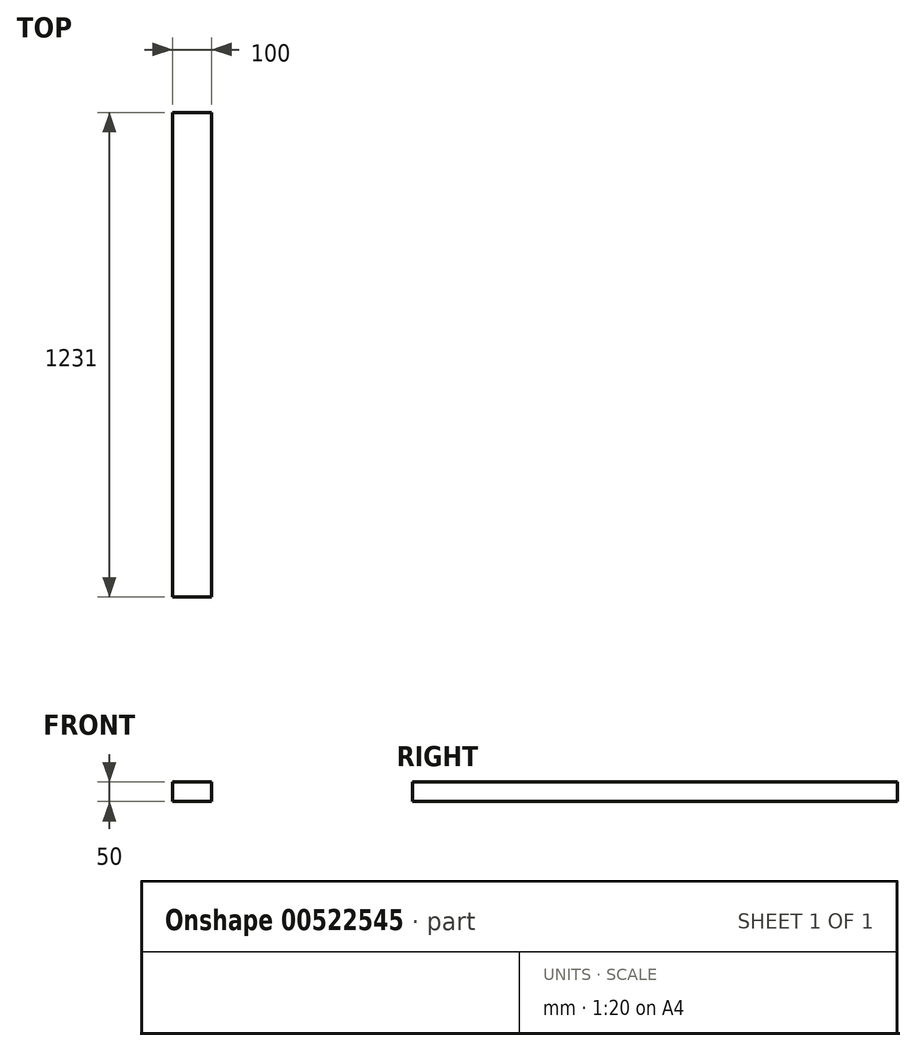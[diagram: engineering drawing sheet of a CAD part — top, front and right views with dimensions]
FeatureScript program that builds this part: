
annotation { "Feature Type Name" : "Feature", "Feature Type Description" : "" }
export const myFeature = defineFeature(function(context is Context, id is Id, definition is map)
    precondition{}
    {
        {
            var Q0;
            Q0=qCreatedBy(makeId("Front.planeOp"),FACE);
            var sketch = newSketch(context, id + "F0", { "sketchPlane" : qUnion([Q0])});
            skLineSegment(sketch, "E0.bottom", {"start": v(-139.39, 44.33) * mm, "end": v(-39.39, 44.33) * mm});
            skLineSegment(sketch, "E0.top", {"start": v(-139.39, -5.67) * mm, "end": v(-39.39, -5.67) * mm});
            skLineSegment(sketch, "E0.left", {"start": v(-139.39, 44.33) * mm, "end": v(-139.39, -5.67) * mm});
            skLineSegment(sketch, "E0.right", {"start": v(-39.39, 44.33) * mm, "end": v(-39.39, -5.67) * mm});
            skSolve(sketch);
        }
        {
            var Q0;
            Q0=qSketchRegion(id+"F0",true);
            extrude(context, id + "F1", {"entities" : qUnion([Q0]), "depth" : 1231 * mm, "offsetDistance" : 25 * mm});
        }
    });
